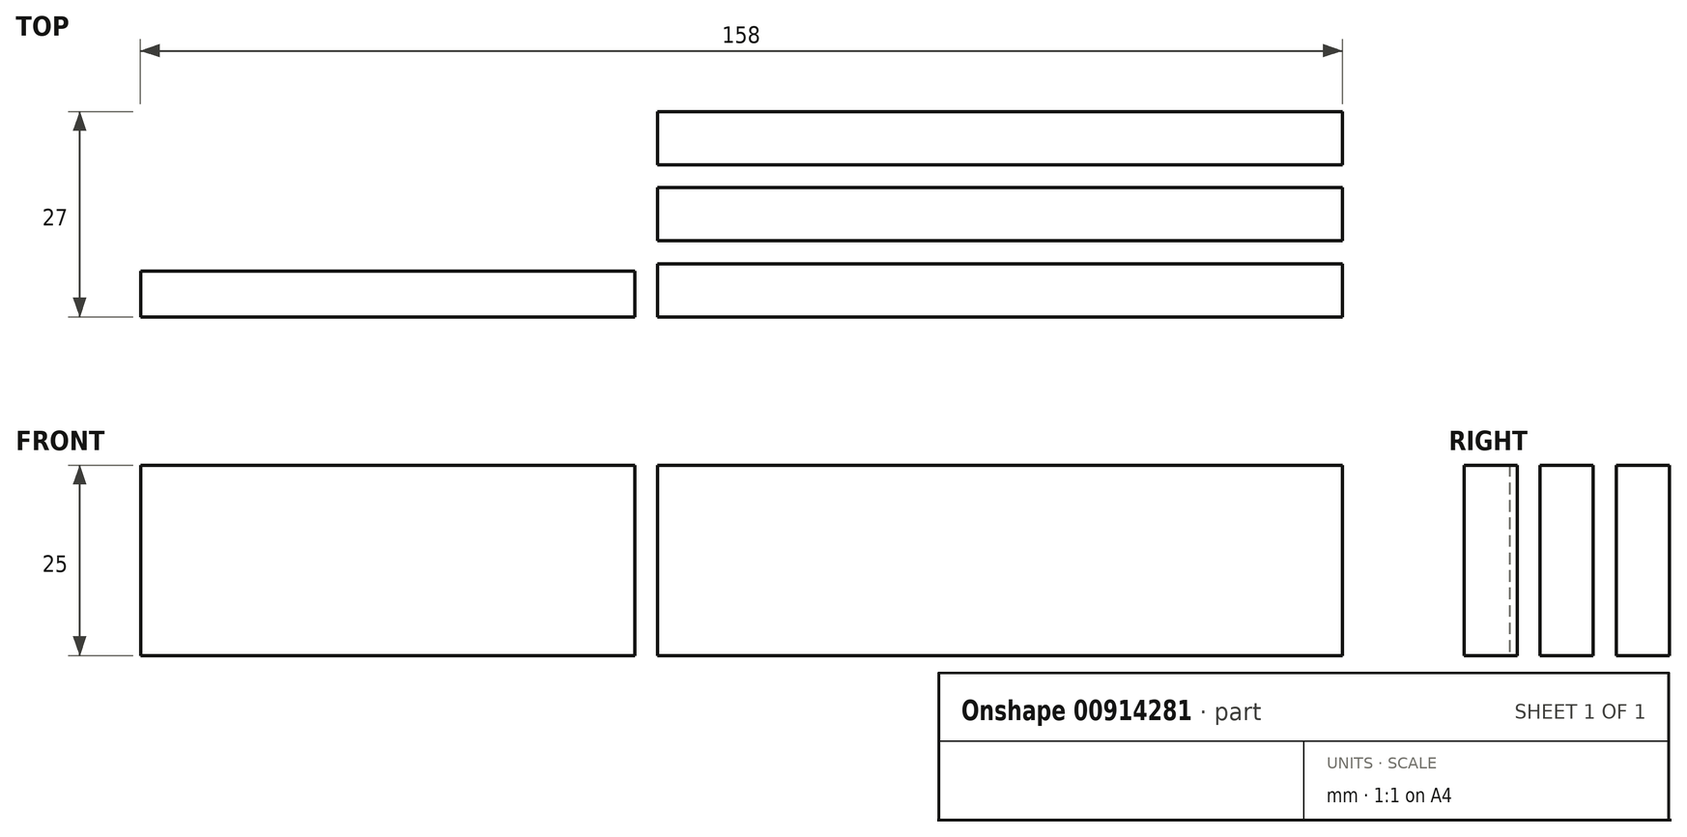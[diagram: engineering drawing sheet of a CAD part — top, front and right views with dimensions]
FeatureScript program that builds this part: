
annotation { "Feature Type Name" : "Feature", "Feature Type Description" : "" }
export const myFeature = defineFeature(function(context is Context, id is Id, definition is map)
    precondition{}
    {
        {
            var Q0;
            Q0=qCreatedBy(makeId("Top.planeOp"),FACE);
            var sketch = newSketch(context, id + "F0", { "sketchPlane" : qUnion([Q0])});
            skLineSegment(sketch, "E0.bottom", {"start": v(-49.79, 14.82) * mm, "end": v(40.21, 14.82) * mm});
            skLineSegment(sketch, "E0.top", {"start": v(-49.79, 7.82) * mm, "end": v(40.21, 7.82) * mm});
            skLineSegment(sketch, "E0.left", {"start": v(-49.79, 14.82) * mm, "end": v(-49.79, 7.82) * mm});
            skLineSegment(sketch, "E0.right", {"start": v(40.21, 14.82) * mm, "end": v(40.21, 7.82) * mm});
            skLineSegment(sketch, "E1.0.1.0", {"start": v(-49.79, 4.82) * mm, "end": v(40.21, 4.82) * mm});
            skLineSegment(sketch, "E1.0.1.1", {"start": v(-49.79, -2.18) * mm, "end": v(40.21, -2.18) * mm});
            skLineSegment(sketch, "E1.0.1.2", {"start": v(40.21, 4.82) * mm, "end": v(40.21, -2.18) * mm});
            skLineSegment(sketch, "E1.0.1.3", {"start": v(-49.79, 4.82) * mm, "end": v(-49.79, -2.18) * mm});
            skLineSegment(sketch, "E1.0.2.0", {"start": v(-49.79, -5.18) * mm, "end": v(40.21, -5.18) * mm});
            skLineSegment(sketch, "E1.0.2.1", {"start": v(-49.79, -12.18) * mm, "end": v(40.21, -12.18) * mm});
            skLineSegment(sketch, "E1.0.2.2", {"start": v(40.21, -5.18) * mm, "end": v(40.21, -12.18) * mm});
            skLineSegment(sketch, "E1.0.2.3", {"start": v(-49.79, -5.18) * mm, "end": v(-49.79, -12.18) * mm});
            skLineSegment(sketch, "E1.direction1", {"start": v(-49.79, 14.82) * mm, "end": v(-24.79, 14.82) * mm, "construction": true});
            skLineSegment(sketch, "E1.direction2", {"start": v(-49.79, 14.82) * mm, "end": v(-49.79, 4.82) * mm, "construction": true});
            skLineSegment(sketch, "E2.bottom", {"start": v(-49.79, -12.18) * mm, "end": v(15.21, -12.18) * mm});
            skLineSegment(sketch, "E3.bottom", {"start": v(-52.79, -12.18) * mm, "end": v(-117.79, -12.18) * mm});
            skLineSegment(sketch, "E3.top", {"start": v(-52.79, -6.18) * mm, "end": v(-117.79, -6.18) * mm});
            skLineSegment(sketch, "E3.left", {"start": v(-52.79, -12.18) * mm, "end": v(-52.79, -6.18) * mm});
            skLineSegment(sketch, "E3.right", {"start": v(-117.79, -12.18) * mm, "end": v(-117.79, -6.18) * mm});
            skSolve(sketch);
        }
        {
            var Q0;
            Q0=makeQuery(id+"F0.imprint","IMPRINT",FACE,{"disambiguationData":[TD([[makeQuery(id+"F0.imprint","IMPRINT",EDGE,{"derivedFrom":sQuery(id+"F0.wireOp",EDGE,"E1.0.1.0")}),-1.0]])]});
            var Q1;
            Q1=makeQuery(id+"F0.imprint","IMPRINT",FACE,{"disambiguationData":[TD([[makeQuery(id+"F0.imprint","IMPRINT",EDGE,{"derivedFrom":sQuery(id+"F0.wireOp",EDGE,"E2.bottom")}),-1.0]])]});
            var Q2;
            Q2=makeQuery(id+"F0.imprint","IMPRINT",FACE,{"disambiguationData":[TD([[makeQuery(id+"F0.imprint","IMPRINT",EDGE,{"derivedFrom":sQuery(id+"F0.wireOp",EDGE,"gsKce2Kj-HUcO-YrFJ-kdgC-verBWYRhqDGa.bottom")}),-1.0]])]});
            var Q3;
            Q3=makeQuery(id+"F0.imprint","IMPRINT",FACE,{"disambiguationData":[TD([[makeQuery(id+"F0.imprint","IMPRINT",EDGE,{"derivedFrom":sQuery(id+"F0.wireOp",EDGE,"E3.bottom")}),-1.0]])]});
            extrude(context, id + "F1", {"entities" : qUnion([Q0, Q1, Q2, Q3]), "depth" : 25 * mm, "offsetDistance" : 25 * mm});
        }
        {
            var Q0;
            Q0=makeQuery(id+"F0.imprint","IMPRINT",FACE,{"disambiguationData":[TD([[makeQuery(id+"F0.imprint","IMPRINT",EDGE,{"derivedFrom":sQuery(id+"F0.wireOp",EDGE,"E0.bottom")}),-1.0]])]});
            var Q1;
            Q1=makeQuery(id+"F0.imprint","IMPRINT",FACE,{"disambiguationData":[TD([[makeQuery(id+"F0.imprint","IMPRINT",EDGE,{"derivedFrom":sQuery(id+"F0.wireOp",EDGE,"E1.0.2.0")}),-1.0]])]});
            extrude(context, id + "F2", {"entities" : qUnion([Q0, Q1]), "depth" : 25 * mm, "offsetDistance" : 25 * mm});
        }
    });
